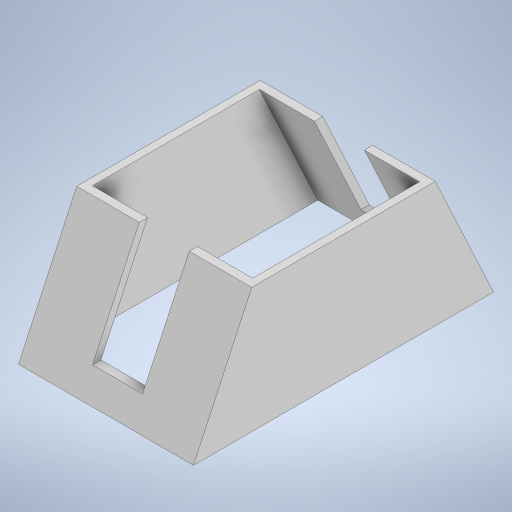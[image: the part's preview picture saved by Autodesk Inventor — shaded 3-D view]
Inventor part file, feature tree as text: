
AUTODESK INVENTOR PART (.ipt)
format: ipt  version: 2023 (Build 270158000, 158)  size: 551,936 bytes
history: native  units: mm
features: extrude x2, sketch x2, shell x1
ambient origin geometry x8: Origin, YZ Plane, XZ Plane, XY Plane, X Axis, Y Axis, Z Axis, Center Point
bodies: Solid1 (feature_tree)
feature tree (5):
  extrude  "Extrusion1"  Depth=120.0mm
  shell  "Shell1"  Thickness=11.34464mm
  extrude  "Extrusion2"  Depth=50.0mm
  sketch  "Sketch1"  dims[d0=120.0mm d1=11.34464mm d2=11.34464mm]
  sketch  "Sketch2"  dims[d3=50.0mm d4=50.0mm d5=70.0mm d6=0.0mm d7=3.0mm d8=10.0mm d9=10.0mm d10=20.0mm d11=40.0mm d12=0.0mm]
